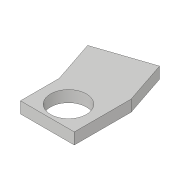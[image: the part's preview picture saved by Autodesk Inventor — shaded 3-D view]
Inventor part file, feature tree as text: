
AUTODESK INVENTOR PART (.ipt)
format: ipt  version: 2018.3 (Build 223284000, 284)  size: 117,248 bytes
history: native  units: in
note: dims shown in document units (in); Inventor stores cm internally (conversion verified against a paired STEP export)
features: extrude x2, fillet x1, sketch x1
ambient origin geometry x8: Origin, YZ Plane, XZ Plane, XY Plane, X Axis, Y Axis, Z Axis, Center Point
bodies: Solid1 (feature_tree)
feature tree (4):
  extrude  "Extrusion1"  Depth=0.875in
  extrude  "Extrusion2"  Depth=1.1003in
  fillet  "Fillet1"  Radius=1.0432in
  sketch  "Sketch1"  dims[d0=0.75in d1=0.875in d2=1.1003in d3=1.0432in d4=0.6925in d5=0.22in d6=0.0in d7=0.0625in d8=0.0in d15=0.126in d16=0.125in d17=0.126in d18=0.5216in d20=1.1095in d21=0.0625in d22=0.4088in]
